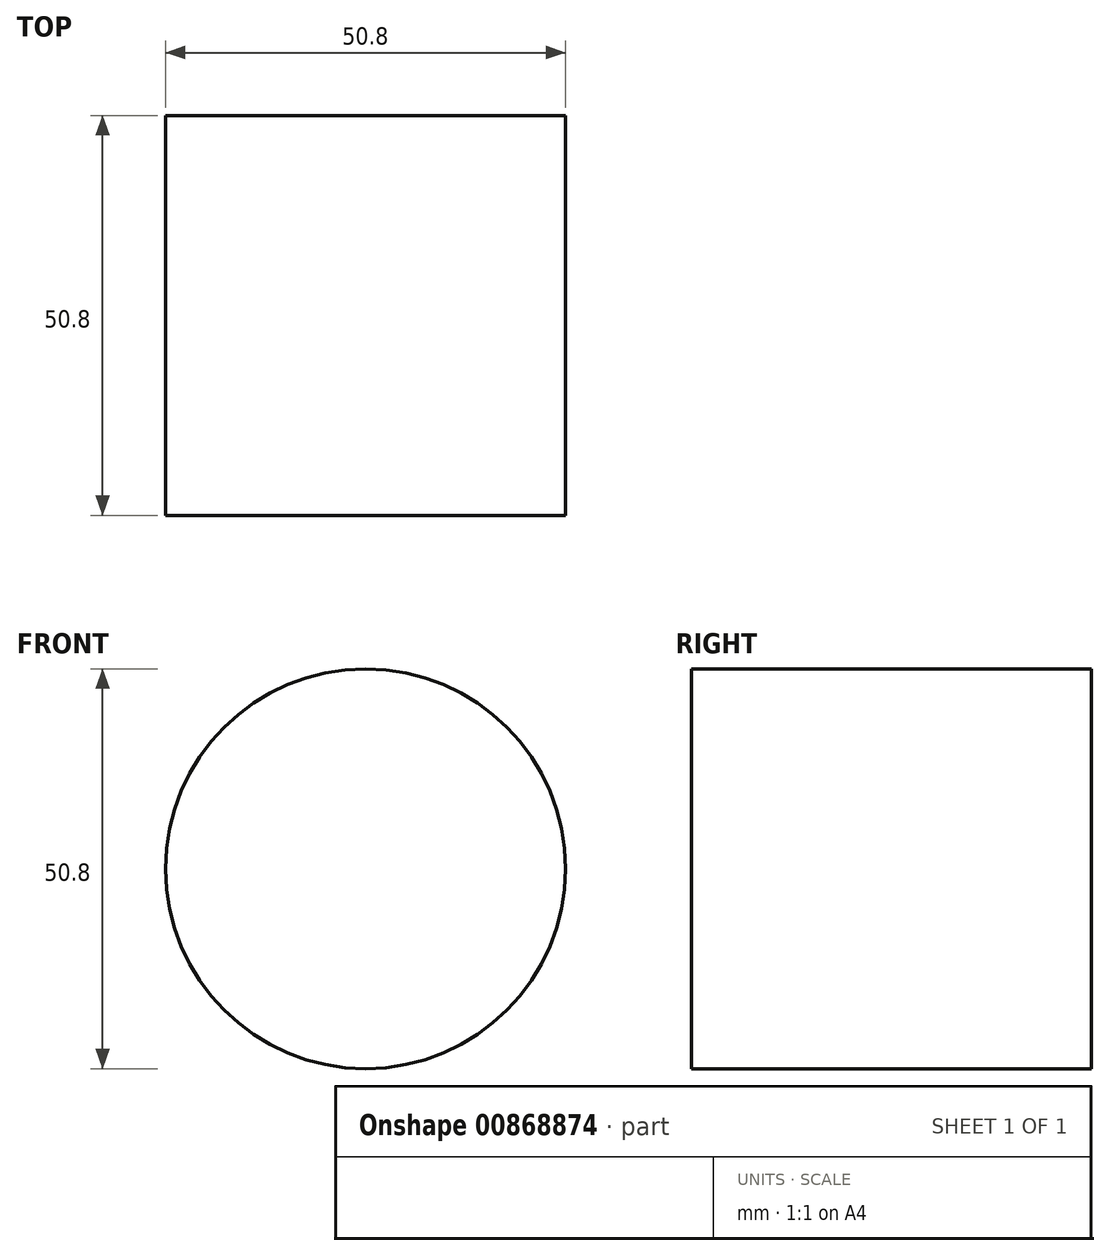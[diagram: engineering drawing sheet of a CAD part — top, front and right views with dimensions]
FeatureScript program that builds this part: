
annotation { "Feature Type Name" : "Feature", "Feature Type Description" : "" }
export const myFeature = defineFeature(function(context is Context, id is Id, definition is map)
    precondition{}
    {
        {
            var Q0;
            Q0=qCreatedBy(makeId("Front.planeOp"),FACE);
            var sketch = newSketch(context, id + "F0", { "sketchPlane" : qUnion([Q0])});
            skCircle(sketch, "E0", {"center": v(0, 0) * mm, "radius": 25.4 * mm});
            skSolve(sketch);
        }
        {
            var Q0;
            Q0 = qSketchRegion(id + "F0", true);
            extrude(context, id + "F1", {"entities" : qUnion([Q0]), "endBound" : BoundingType.SYMMETRIC, "depth" : 50.8 * mm, "offsetDistance" : 25.4 * mm});
        }
        {
            var Q0;
            Q0=qCreatedBy(makeId("Right.planeOp"),FACE);
            var sketch = newSketch(context, id + "F2", { "sketchPlane" : qUnion([Q0])});
            skCircle(sketch, "E1", {"center": v(0, 0) * mm, "radius": 12.23 * mm});
            skSolve(sketch);
        }
        {
            var Q0;
            Q0=sQuery(id+"F2.wireOp",EDGE,"E1");
            extrude(context, id + "F3", {"bodyType" : ToolBodyType.SURFACE, "surfaceEntities" : qUnion([Q0]), "endBound" : BoundingType.THROUGH_ALL, "depth" : 50.8 * mm, "offsetDistance" : 25.4 * mm});
        }
    });
